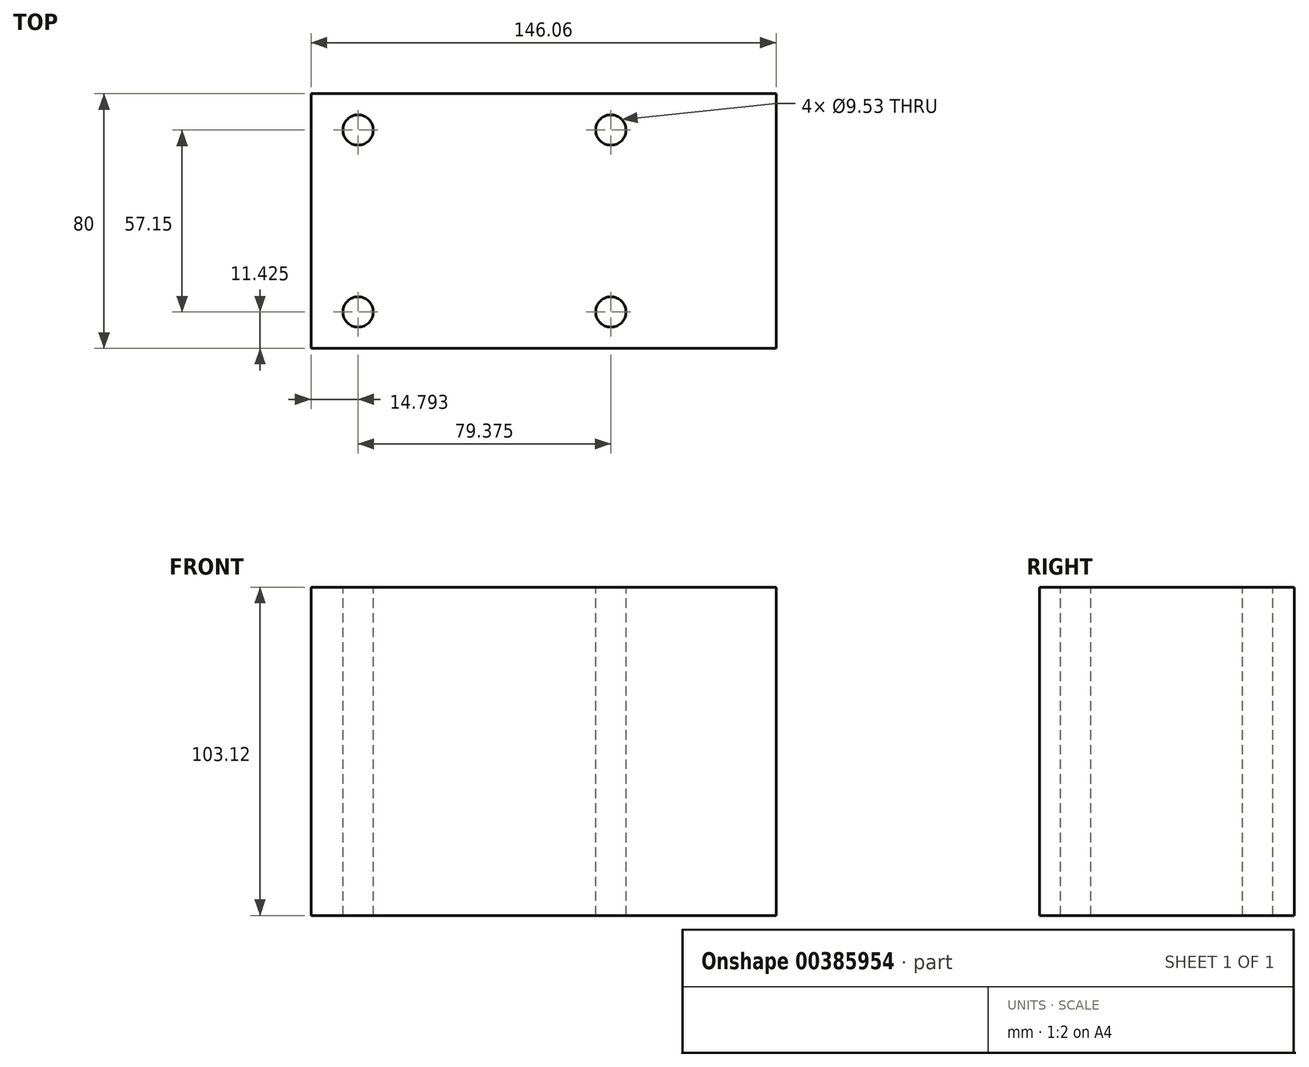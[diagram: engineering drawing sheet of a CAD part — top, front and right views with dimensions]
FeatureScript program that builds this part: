
annotation { "Feature Type Name" : "Feature", "Feature Type Description" : "" }
export const myFeature = defineFeature(function(context is Context, id is Id, definition is map)
    precondition{}
    {
        {
            var Q0;
            Q0=qCreatedBy(makeId("Top.planeOp"),FACE);
            var sketch = newSketch(context, id + "F0", { "sketchPlane" : qUnion([Q0])});
            skLineSegment(sketch, "E0.bottom", {"start": v(73.03, -40) * mm, "end": v(-73.02, -40) * mm});
            skLineSegment(sketch, "E0.top", {"start": v(73.02, 40) * mm, "end": v(-73.03, 40) * mm});
            skLineSegment(sketch, "E0.left", {"start": v(73.03, -40) * mm, "end": v(73.02, 40) * mm});
            skLineSegment(sketch, "E0.right", {"start": v(-73.03, -40) * mm, "end": v(-73.03, 40) * mm});
            skPoint(sketch, "E0.middle", {"position": v(0, 0) * mm});
            skSolve(sketch);
        }
        {
            var Q0;
            Q0 = qSketchRegion(id + "F0", true);
            extrude(context, id + "F1", {"entities" : qUnion([Q0]), "depth" : 103.12 * mm});
        }
        {
            var Q0;
            Q0=makeQuery(id+"F1.opExtrude","CAP_FACE",FACE,{"disambiguationData":[OSD([sQuery(id+"F0.wireOp",EDGE,"E0.bottom"),sQuery(id+"F0.wireOp",EDGE,"E0.top"),sQuery(id+"F0.wireOp",EDGE,"E0.left"),sQuery(id+"F0.wireOp",EDGE,"E0.right")])],"isStart":false});
            var sketch = newSketch(context, id + "F2", { "sketchPlane" : qUnion([Q0])});
            skLineSegment(sketch, "E1.bottom", {"start": v(33.84, -39.69) * mm, "end": v(-70.94, -39.69) * mm, "construction": true});
            skLineSegment(sketch, "E1.top", {"start": v(33.84, 39.69) * mm, "end": v(-70.94, 39.69) * mm, "construction": true});
            skLineSegment(sketch, "E1.left", {"start": v(33.84, -39.69) * mm, "end": v(33.84, 39.69) * mm, "construction": true});
            skLineSegment(sketch, "E1.right", {"start": v(-70.94, -39.69) * mm, "end": v(-70.94, 39.69) * mm, "construction": true});
            skPoint(sketch, "E1.middle", {"position": v(-18.55, 0) * mm});
            skLineSegment(sketch, "E2", {"start": v(-70.94, 0) * mm, "end": v(33.84, 0) * mm, "construction": true});
            skPoint(sketch, "E3.startSnap0", {"position": v(73.03, 0) * mm});
            skPoint(sketch, "E3.endSnap0", {"position": v(-73.03, 0) * mm});
            skLineSegment(sketch, "E4", {"start": v(73.03, 0) * mm, "end": v(-73.03, 0) * mm, "construction": true});
            skCircle(sketch, "E5", {"center": v(-58.24, 28.57) * mm, "radius": 4.76 * mm});
            skCircle(sketch, "E6", {"center": v(21.14, 28.57) * mm, "radius": 4.76 * mm});
            skCircle(sketch, "E7.MirrorC", {"center": v(-58.24, -28.57) * mm, "radius": 4.76 * mm});
            skCircle(sketch, "E8.MirrorC", {"center": v(21.14, -28.57) * mm, "radius": 4.76 * mm});
            skSolve(sketch);
        }
        {
            var Q0;
            Q0 = qSketchRegion(id + "F2", true);
            extrude(context, id + "F3", {"entities" : qUnion([Q0]), "operationType" : NewBodyOperationType.REMOVE, "endBound" : BoundingType.THROUGH_ALL, "oppositeDirection" : true, "depth" : 25.4 * mm});
        }
    });
